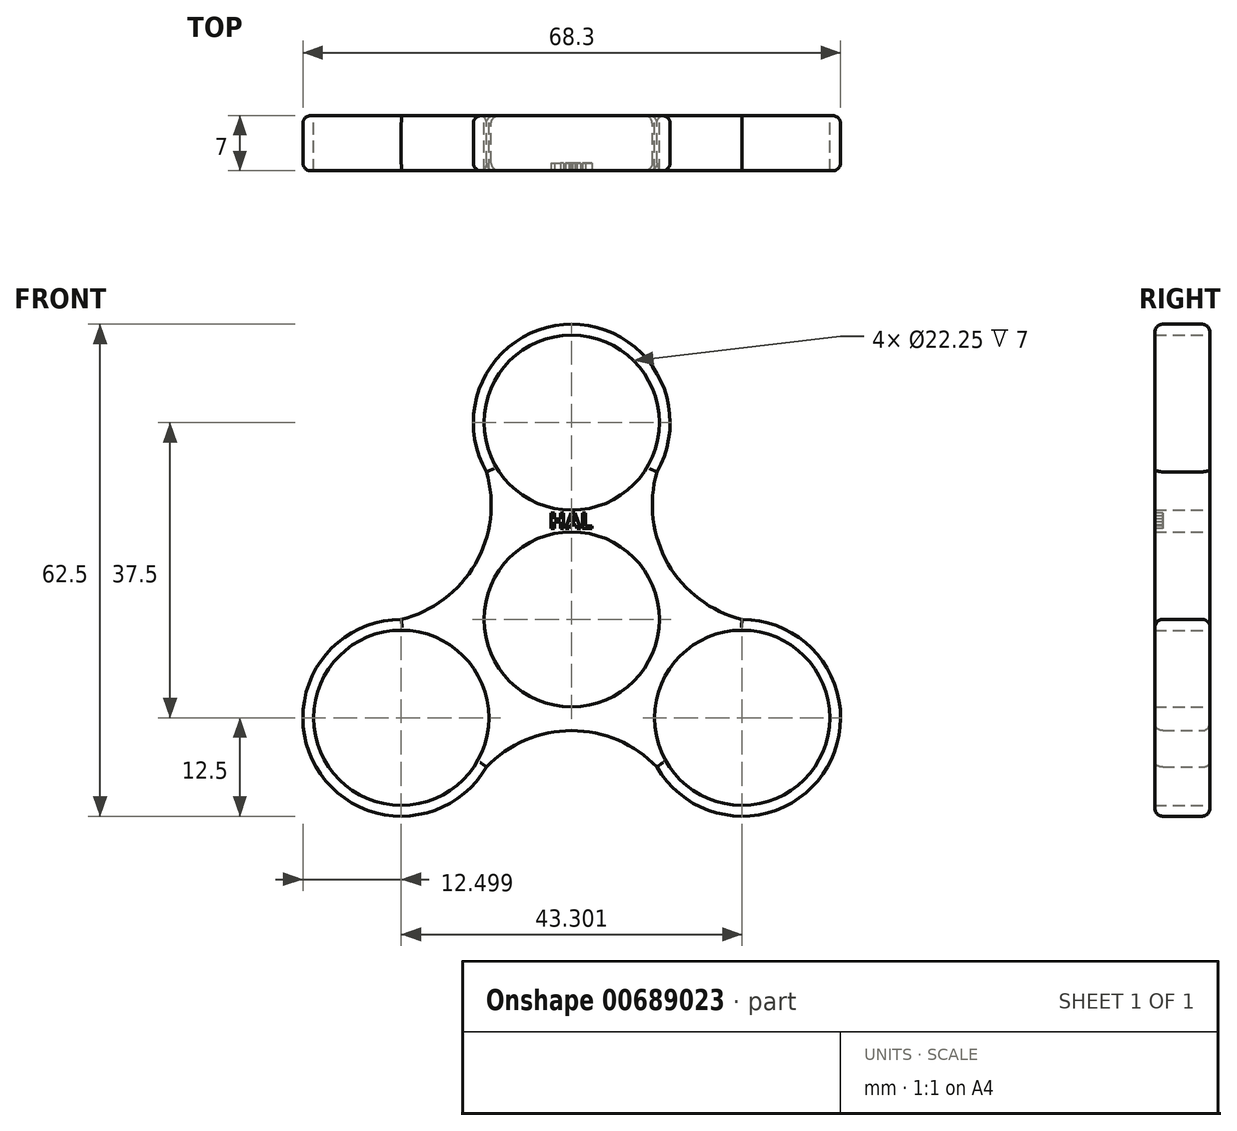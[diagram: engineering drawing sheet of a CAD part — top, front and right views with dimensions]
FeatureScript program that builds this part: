
annotation { "Feature Type Name" : "Feature", "Feature Type Description" : "" }
export const myFeature = defineFeature(function(context is Context, id is Id, definition is map)
    precondition{}
    {
        {
            var Q0;
            Q0=qCreatedBy(makeId("Front.planeOp"),FACE);
            var sketch = newSketch(context, id + "F0", { "sketchPlane" : qUnion([Q0])});
            skCircle(sketch, "E0", {"center": v(0, 0) * mm, "radius": 11.12 * mm});
            skCircle(sketch, "E1", {"center": v(0, 25) * mm, "radius": 11.12 * mm});
            skCircle(sketch, "E2", {"center": v(21.65, -12.5) * mm, "radius": 11.12 * mm});
            skCircle(sketch, "E3", {"center": v(-21.65, -12.5) * mm, "radius": 11.12 * mm});
            skArc(sketch, "E4", {"start": v(10.83, 18.75) * mm, "mid": v(0, 37.5) * mm, "end": v(-10.83, 18.75) * mm});
            skArc(sketch, "E5", {"start": v(10.83, -18.75) * mm, "mid": v(32.48, -18.75) * mm, "end": v(21.65, 0) * mm});
            skArc(sketch, "E6", {"start": v(-21.65, 0) * mm, "mid": v(-32.48, -18.75) * mm, "end": v(-10.83, -18.75) * mm});
            skLineSegment(sketch, "E7", {"start": v(9.63, 19.44) * mm, "end": v(13, 17.5) * mm});
            skLineSegment(sketch, "E8", {"start": v(-21.65, -1.37) * mm, "end": v(-21.65, 2.5) * mm});
            skArc(sketch, "E9", {"start": v(-21.65, 0) * mm, "mid": v(-12.24, 7.07) * mm, "end": v(-10.83, 18.75) * mm});
            skArc(sketch, "E10", {"start": v(10.83, 18.75) * mm, "mid": v(12.24, 7.07) * mm, "end": v(21.65, 0) * mm});
            skArc(sketch, "E11", {"start": v(10.83, -18.75) * mm, "mid": v(0, -14.13) * mm, "end": v(-10.83, -18.75) * mm});
            skSolve(sketch);
        }
        {
            var Q0;
            Q0=makeQuery(id+"F0.imprint","IMPRINT",FACE,{"disambiguationData":[TD([[makeQuery(id+"F0.imprint","IMPRINT",EDGE,{"derivedFrom":sQuery(id+"F0.wireOp",EDGE,"E0")}),-1.0]])]});
            extrude(context, id + "F1", {"entities" : qUnion([Q0]), "depth" : 7 * mm, "offsetDistance" : 25 * mm});
        }
        {
            var Q0;
            Q0=makeQuery(id+"F1.opExtrude","CAP_EDGE",EDGE,{"disambiguationData":[OSD([sQuery(id+"F0.wireOp",EDGE,"E4")])],"isStart":false});
            var Q1;
            Q1=makeQuery(id+"F1.opExtrude","CAP_EDGE",EDGE,{"disambiguationData":[OSD([sQuery(id+"F0.wireOp",EDGE,"E9")])],"isStart":false});
            var Q2;
            Q2=makeQuery(id+"F1.opExtrude","CAP_EDGE",EDGE,{"disambiguationData":[OSD([sQuery(id+"F0.wireOp",EDGE,"E6")])],"isStart":false});
            var Q3;
            Q3=makeQuery(id+"F1.opExtrude","CAP_EDGE",EDGE,{"disambiguationData":[OSD([sQuery(id+"F0.wireOp",EDGE,"E11")])],"isStart":false});
            var Q4;
            Q4=makeQuery(id+"F1.opExtrude","CAP_EDGE",EDGE,{"disambiguationData":[OSD([sQuery(id+"F0.wireOp",EDGE,"E5")])],"isStart":false});
            var Q5;
            Q5=makeQuery(id+"F1.opExtrude","CAP_EDGE",EDGE,{"disambiguationData":[OSD([sQuery(id+"F0.wireOp",EDGE,"E10")])],"isStart":false});
            fillet(context, id + "F2", {"entities" : qUnion([Q0, Q1, Q2, Q3, Q4, Q5]), "radius" : 1 * mm, "tangentPropagation" : true, "allowEdgeOverflow" : false});
        }
        {
            var Q0;
            Q0=makeQuery(id+"F1.opExtrude","CAP_EDGE",EDGE,{"disambiguationData":[OSD([sQuery(id+"F0.wireOp",EDGE,"E4")])],"isStart":true});
            var Q1;
            Q1=makeQuery(id+"F1.opExtrude","CAP_EDGE",EDGE,{"disambiguationData":[OSD([sQuery(id+"F0.wireOp",EDGE,"E10")])],"isStart":true});
            var Q2;
            Q2=makeQuery(id+"F1.opExtrude","CAP_EDGE",EDGE,{"disambiguationData":[OSD([sQuery(id+"F0.wireOp",EDGE,"E5")])],"isStart":true});
            var Q3;
            Q3=makeQuery(id+"F1.opExtrude","CAP_EDGE",EDGE,{"disambiguationData":[OSD([sQuery(id+"F0.wireOp",EDGE,"E11")])],"isStart":true});
            var Q4;
            Q4=makeQuery(id+"F1.opExtrude","CAP_EDGE",EDGE,{"disambiguationData":[OSD([sQuery(id+"F0.wireOp",EDGE,"E6")])],"isStart":true});
            var Q5;
            Q5=makeQuery(id+"F1.opExtrude","CAP_EDGE",EDGE,{"disambiguationData":[OSD([sQuery(id+"F0.wireOp",EDGE,"E9")])],"isStart":true});
            fillet(context, id + "F3", {"entities" : qUnion([Q0, Q1, Q2, Q3, Q4, Q5]), "radius" : 1 * mm, "tangentPropagation" : true, "allowEdgeOverflow" : false});
        }
        {
            var Q0;
            Q0=makeQuery(id+"F1.opExtrude","CAP_FACE",FACE,{"disambiguationData":[OSD([sQuery(id+"F0.wireOp",EDGE,"E0"),sQuery(id+"F0.wireOp",EDGE,"E1"),sQuery(id+"F0.wireOp",EDGE,"E2"),sQuery(id+"F0.wireOp",EDGE,"E3"),sQuery(id+"F0.wireOp",EDGE,"E4"),sQuery(id+"F0.wireOp",EDGE,"E5"),sQuery(id+"F0.wireOp",EDGE,"E6"),sQuery(id+"F0.wireOp",EDGE,"E9"),sQuery(id+"F0.wireOp",EDGE,"E10"),sQuery(id+"F0.wireOp",EDGE,"E11")])],"isStart":false});
            var sketch = newSketch(context, id + "F4", { "sketchPlane" : qUnion([Q0])});
            skText(sketch, "E12", { "text": "HAL", "fontName": "OpenSans-Bold.ttf"});
            const initialGuessF4  = {"E12": [-0.00286, 0.01155, 1, 0, 0.00196]};
            skSetInitialGuess(sketch, initialGuessF4);
            skSolve(sketch);
        }
        {
            var Q0;
            Q0 = qSketchRegion(id + "F4", true);
            extrude(context, id + "F5", {"entities" : qUnion([Q0]), "operationType" : NewBodyOperationType.REMOVE, "oppositeDirection" : true, "depth" : 1 * mm, "offsetDistance" : 25 * mm});
        }
    });
